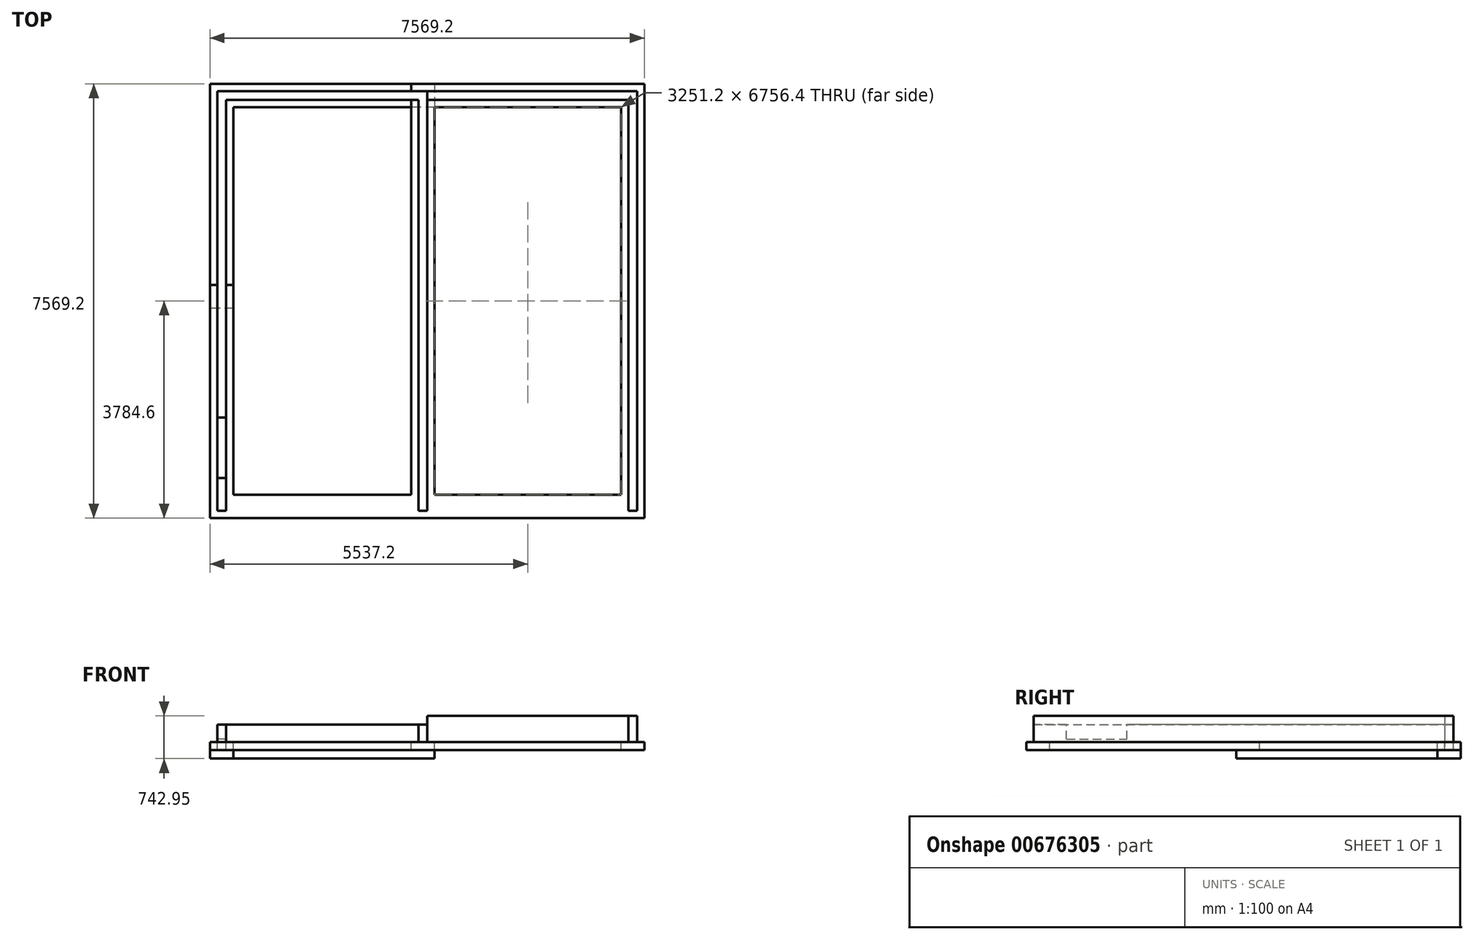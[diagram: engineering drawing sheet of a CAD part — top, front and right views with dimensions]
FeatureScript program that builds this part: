
annotation { "Feature Type Name" : "Feature", "Feature Type Description" : "" }
export const myFeature = defineFeature(function(context is Context, id is Id, definition is map)
    precondition{}
    {
        {
            var Q0;
            Q0=qCreatedBy(makeId("Top.planeOp"),FACE);
            var sketch = newSketch(context, id + "F0", { "sketchPlane" : qUnion([Q0])});
            skLineSegment(sketch, "E0.bottom", {"start": v(-3657.6, 3657.6) * mm, "end": v(3657.6, 3657.6) * mm});
            skLineSegment(sketch, "E0.top", {"start": v(-3657.6, -3657.6) * mm, "end": v(3657.6, -3657.6) * mm, "construction": true});
            skLineSegment(sketch, "E0.left", {"start": v(-3657.6, 3657.6) * mm, "end": v(-3657.6, -3657.6) * mm});
            skLineSegment(sketch, "E0.right", {"start": v(3657.6, 3657.6) * mm, "end": v(3657.6, -3657.6) * mm});
            skPoint(sketch, "E0.middle", {"position": v(0, 0) * mm});
            skLineSegment(sketch, "E1.0", {"start": v(-3505.2, 3505.2) * mm, "end": v(-3505.2, -3657.6) * mm});
            skLineSegment(sketch, "E1.1", {"start": v(-3505.2, 3505.2) * mm, "end": v(-152.4, 3505.2) * mm});
            skLineSegment(sketch, "E1.2", {"start": v(3505.2, 3505.2) * mm, "end": v(3505.2, -3657.6) * mm});
            skLineSegment(sketch, "E2", {"start": v(-3657.6, -3657.6) * mm, "end": v(-3505.2, -3657.6) * mm});
            skLineSegment(sketch, "E3", {"start": v(3657.6, -3657.6) * mm, "end": v(3505.2, -3657.6) * mm});
            skLineSegment(sketch, "E4", {"start": v(0, 3505.2) * mm, "end": v(0, -3657.6) * mm});
            skLineSegment(sketch, "E5", {"start": v(0, -3657.6) * mm, "end": v(-152.4, -3657.6) * mm});
            skLineSegment(sketch, "E6", {"start": v(-152.4, -3657.6) * mm, "end": v(-152.4, 3505.2) * mm});
            skLineSegment(sketch, "E7.trimOffspring", {"start": v(0, 3505.2) * mm, "end": v(3505.2, 3505.2) * mm});
            skSolve(sketch);
        }
        {
            var Q0;
            Q0=makeQuery(id+"F0.imprint","IMPRINT",FACE,{"disambiguationData":[TD([[makeQuery(id+"F0.imprint","IMPRINT",EDGE,{"derivedFrom":sQuery(id+"F0.wireOp",EDGE,"E0.bottom")}),-1.0]])]});
            extrude(context, id + "F1", {"entities" : qUnion([Q0]), "depth" : 152.4 * mm, "offsetDistance" : 25.4 * mm});
        }
        {
            var Q0;
            Q0=makeQuery(id+"F1.opExtrude","CAP_FACE",FACE,{"disambiguationData":[OSD([sQuery(id+"F0.wireOp",EDGE,"E0.bottom"),sQuery(id+"F0.wireOp",EDGE,"E0.left"),sQuery(id+"F0.wireOp",EDGE,"E0.right"),sQuery(id+"F0.wireOp",EDGE,"E1.0"),sQuery(id+"F0.wireOp",EDGE,"E1.1"),sQuery(id+"F0.wireOp",EDGE,"E1.2"),sQuery(id+"F0.wireOp",EDGE,"E2"),sQuery(id+"F0.wireOp",EDGE,"E3")])],"isStart":true});
            extrude(context, id + "F2", {"entities" : qUnion([Q0]), "operationType" : NewBodyOperationType.ADD, "depth" : 152.4 * mm, "offsetDistance" : 25.4 * mm});
        }
        {
            var Q0;
            Q0=makeQuery(id+"F2.opExtrude","CAP_FACE",FACE,{"disambiguationData":[OSD([sQuery(id+"F0.wireOp",EDGE,"E0.bottom"),sQuery(id+"F0.wireOp",EDGE,"E0.left"),sQuery(id+"F0.wireOp",EDGE,"E0.right"),sQuery(id+"F0.wireOp",EDGE,"E1.0"),sQuery(id+"F0.wireOp",EDGE,"E1.1"),sQuery(id+"F0.wireOp",EDGE,"E1.2"),sQuery(id+"F0.wireOp",EDGE,"E2"),sQuery(id+"F0.wireOp",EDGE,"E3")])],"isStart":false});
            var sketch = newSketch(context, id + "F3", { "sketchPlane" : qUnion([Q0])});
            skLineSegment(sketch, "E8.bottom", {"start": v(-3784.6, 3784.6) * mm, "end": v(3784.6, 3784.6) * mm});
            skLineSegment(sketch, "E8.top", {"start": v(-3784.6, -3784.6) * mm, "end": v(3784.6, -3784.6) * mm, "construction": true});
            skLineSegment(sketch, "E8.left", {"start": v(-3784.6, 3784.6) * mm, "end": v(-3784.6, -3784.6) * mm, "construction": true});
            skLineSegment(sketch, "E8.right", {"start": v(3784.6, 3784.6) * mm, "end": v(3784.6, -3784.6) * mm});
            skPoint(sketch, "E8.middle", {"position": v(0, 0) * mm});
            skLineSegment(sketch, "E9.0", {"start": v(-3378.2, 3378.2) * mm, "end": v(-279.4, 3378.2) * mm});
            skLineSegment(sketch, "E9.1", {"start": v(-3378.2, 3378.2) * mm, "end": v(-3378.2, -279.4) * mm});
            skLineSegment(sketch, "E9.3", {"start": v(3378.2, 3378.2) * mm, "end": v(3378.2, -3378.2) * mm});
            skLineSegment(sketch, "E10", {"start": v(-279.4, 3378.2) * mm, "end": v(-279.4, -3505.2) * mm});
            skLineSegment(sketch, "E11", {"start": v(127, 3378.2) * mm, "end": v(127, -3378.2) * mm});
            skLineSegment(sketch, "E12.trimOffspring", {"start": v(127, 3378.2) * mm, "end": v(3378.2, 3378.2) * mm});
            skLineSegment(sketch, "E13.trimOffspring", {"start": v(127, -3378.2) * mm, "end": v(3378.2, -3378.2) * mm});
            skLineSegment(sketch, "E14", {"start": v(-279.4, -3505.2) * mm, "end": v(-3505.2, -3505.2) * mm});
            skLineSegment(sketch, "E15", {"start": v(-3784.6, 3784.6) * mm, "end": v(-3784.6, -279.4) * mm});
            skLineSegment(sketch, "E16", {"start": v(-3784.6, -279.4) * mm, "end": v(-3657.6, -279.4) * mm});
            skLineSegment(sketch, "E17", {"start": v(-3657.6, -279.4) * mm, "end": v(-3657.6, -3657.6) * mm});
            skLineSegment(sketch, "E18", {"start": v(-3657.6, -3657.6) * mm, "end": v(-279.4, -3657.6) * mm});
            skLineSegment(sketch, "E19", {"start": v(-279.4, -3657.6) * mm, "end": v(-279.4, -3784.6) * mm});
            skLineSegment(sketch, "E20", {"start": v(-279.4, -3784.6) * mm, "end": v(3784.6, -3784.6) * mm});
            skLineSegment(sketch, "E21", {"start": v(-3505.2, -279.4) * mm, "end": v(-3378.2, -279.4) * mm});
            skLineSegment(sketch, "E22", {"start": v(-3505.2, -279.4) * mm, "end": v(-3505.2, -3505.2) * mm});
            skSolve(sketch);
        }
        {
            var Q0;
            Q0 = qSketchRegion(id + "F3", true);
            extrude(context, id + "F4", {"entities" : qUnion([Q0]), "operationType" : NewBodyOperationType.ADD, "depth" : 139.7 * mm, "offsetDistance" : 25.4 * mm});
        }
        {
            var Q0;
            Q0=makeQuery(id+"F1.opExtrude","CAP_FACE",FACE,{"disambiguationData":[OSD([sQuery(id+"F0.wireOp",EDGE,"E0.bottom"),sQuery(id+"F0.wireOp",EDGE,"E0.left"),sQuery(id+"F0.wireOp",EDGE,"E0.right"),sQuery(id+"F0.wireOp",EDGE,"E1.0"),sQuery(id+"F0.wireOp",EDGE,"E1.1"),sQuery(id+"F0.wireOp",EDGE,"E1.2"),sQuery(id+"F0.wireOp",EDGE,"E2"),sQuery(id+"F0.wireOp",EDGE,"E3"),sQuery(id+"F0.wireOp",EDGE,"E4"),sQuery(id+"F0.wireOp",EDGE,"E5"),sQuery(id+"F0.wireOp",EDGE,"E6"),sQuery(id+"F0.wireOp",EDGE,"E7.trimOffspring")])],"isStart":false});
            var sketch = newSketch(context, id + "F5", { "sketchPlane" : qUnion([Q0])});
            skLineSegment(sketch, "E23", {"start": v(0, 3657.6) * mm, "end": v(3657.6, 3657.6) * mm});
            skLineSegment(sketch, "E24", {"start": v(3657.6, 3657.6) * mm, "end": v(3657.6, -3657.6) * mm});
            skLineSegment(sketch, "E25", {"start": v(3657.6, -3657.6) * mm, "end": v(3505.2, -3657.6) * mm});
            skLineSegment(sketch, "E26", {"start": v(3505.2, -3657.6) * mm, "end": v(3505.2, 3505.2) * mm});
            skLineSegment(sketch, "E27", {"start": v(3505.2, 3505.2) * mm, "end": v(0, 3505.2) * mm});
            skLineSegment(sketch, "E28", {"start": v(0, 3505.2) * mm, "end": v(0, 3657.6) * mm});
            skSolve(sketch);
        }
        {
            var Q0;
            Q0=makeQuery(id+"F4.opExtrude","CAP_FACE",FACE,{"disambiguationData":[OSD([sQuery(id+"F3.wireOp",EDGE,"E8.bottom"),sQuery(id+"F3.wireOp",EDGE,"E8.right"),sQuery(id+"F3.wireOp",EDGE,"E9.0"),sQuery(id+"F3.wireOp",EDGE,"E9.1"),sQuery(id+"F3.wireOp",EDGE,"E9.3"),sQuery(id+"F3.wireOp",EDGE,"E10"),sQuery(id+"F3.wireOp",EDGE,"E11"),sQuery(id+"F3.wireOp",EDGE,"E12.trimOffspring"),sQuery(id+"F3.wireOp",EDGE,"E13.trimOffspring"),sQuery(id+"F3.wireOp",EDGE,"E14"),sQuery(id+"F3.wireOp",EDGE,"E15"),sQuery(id+"F3.wireOp",EDGE,"E16"),sQuery(id+"F3.wireOp",EDGE,"E17"),sQuery(id+"F3.wireOp",EDGE,"E18"),sQuery(id+"F3.wireOp",EDGE,"E19"),sQuery(id+"F3.wireOp",EDGE,"E20"),sQuery(id+"F3.wireOp",EDGE,"E21"),sQuery(id+"F3.wireOp",EDGE,"E22")])],"isStart":false});
            var sketch = newSketch(context, id + "F6", { "sketchPlane" : qUnion([Q0])});
            skLineSegment(sketch, "E29", {"start": v(-3784.6, 127) * mm, "end": v(-3784.6, -3784.6) * mm});
            skLineSegment(sketch, "E30", {"start": v(-3784.6, -3784.6) * mm, "end": v(127, -3784.6) * mm});
            skLineSegment(sketch, "E31", {"start": v(127, -3784.6) * mm, "end": v(127, -3378.2) * mm});
            skLineSegment(sketch, "E32", {"start": v(127, -3378.2) * mm, "end": v(-3378.2, -3378.2) * mm});
            skLineSegment(sketch, "E33", {"start": v(-3378.2, -3378.2) * mm, "end": v(-3378.2, 127) * mm});
            skLineSegment(sketch, "E34", {"start": v(-3378.2, 127) * mm, "end": v(-3784.6, 127) * mm});
            skSolve(sketch);
        }
        {
            var Q0;
            Q0 = qSketchRegion(id + "F6", true);
            extrude(context, id + "F7", {"entities" : qUnion([Q0]), "operationType" : NewBodyOperationType.ADD, "depth" : 146.05 * mm, "offsetDistance" : 25.4 * mm});
        }
        {
            var Q0;
            Q0 = qSketchRegion(id + "F5", true);
            extrude(context, id + "F8", {"entities" : qUnion([Q0]), "operationType" : NewBodyOperationType.ADD, "depth" : 152.4 * mm, "offsetDistance" : 25.4 * mm});
        }
        {
            var Q0;
            {var subQ0=sQuery(id+"F0.wireOp",EDGE,"E5");Q0=makeQuery(id+"F2.boolean.opBoolean","MERGE",FACE,{"derivedFrom":[makeQuery(id+"F1.opExtrude","SWEPT_FACE",FACE,{"disambiguationData":[OSD([subQ0])]}),makeQuery(id+"F2.opExtrude","SWEPT_FACE",FACE,{"disambiguationData":[OSD([subQ0])]})]});}
            var sketch = newSketch(context, id + "F9", { "sketchPlane" : qUnion([Q0])});
            skLineSegment(sketch, "E35", {"start": v(0, 107.95) * mm, "end": v(-3657.6, -25.4) * mm});
            skLineSegment(sketch, "E36", {"start": v(-3657.6, -25.4) * mm, "end": v(3657.6, -25.4) * mm});
            skLineSegment(sketch, "E37", {"start": v(3657.6, -25.4) * mm, "end": v(3657.6, 273.05) * mm});
            skLineSegment(sketch, "E38", {"start": v(3657.6, 273.05) * mm, "end": v(0, 107.95) * mm});
            skSolve(sketch);
        }
        {
            var Q0;
            {var subQ0=sQuery(id+"F0.wireOp",EDGE,"E0.right");Q0=makeQuery(id+"F8.boolean.opBoolean","MERGE",FACE,{"derivedFrom":[makeQuery(id+"F2.boolean.opBoolean","MERGE",FACE,{"derivedFrom":[makeQuery(id+"F1.opExtrude","SWEPT_FACE",FACE,{"disambiguationData":[OSD([subQ0])]}),makeQuery(id+"F2.opExtrude","SWEPT_FACE",FACE,{"disambiguationData":[OSD([subQ0])]})]}),makeQuery(id+"F8.opExtrude","SWEPT_FACE",FACE,{"disambiguationData":[OSD([sQuery(id+"F5.wireOp",EDGE,"E24")])]})]});}
            var sketch = newSketch(context, id + "F10", { "sketchPlane" : qUnion([Q0])});
            skLineSegment(sketch, "E39", {"start": v(-3657.6, -25.4) * mm, "end": v(3657.6, -25.4) * mm});
            skLineSegment(sketch, "E40", {"start": v(3657.6, -25.4) * mm, "end": v(3657.6, 158.75) * mm});
            skLineSegment(sketch, "E41", {"start": v(3657.6, 158.75) * mm, "end": v(0, 196.85) * mm});
            skLineSegment(sketch, "E42", {"start": v(0, 196.85) * mm, "end": v(-3657.6, 273.05) * mm});
            skLineSegment(sketch, "E43", {"start": v(-3657.6, 273.05) * mm, "end": v(-3657.6, -25.4) * mm});
            skLineSegment(sketch, "E44", {"start": v(0, 196.85) * mm, "end": v(0, -25.4) * mm});
            skSolve(sketch);
        }
        {
            var Q0;
            {var subQ0=sQuery(id+"F0.wireOp",EDGE,"E0.left");Q0=makeQuery(id+"F4.boolean.opBoolean","MERGE",FACE,{"derivedFrom":[makeQuery(id+"F2.boolean.opBoolean","MERGE",FACE,{"derivedFrom":[makeQuery(id+"F1.opExtrude","SWEPT_FACE",FACE,{"disambiguationData":[OSD([subQ0])]}),makeQuery(id+"F2.opExtrude","SWEPT_FACE",FACE,{"disambiguationData":[OSD([subQ0])]})]}),makeQuery(id+"F4.opExtrude","SWEPT_FACE",FACE,{"disambiguationData":[OSD([sQuery(id+"F3.wireOp",EDGE,"E17")])]})]});}
            var sketch = newSketch(context, id + "F11", { "sketchPlane" : qUnion([Q0])});
            skLineSegment(sketch, "E45", {"start": v(3657.6, -25.4) * mm, "end": v(0, -88.9) * mm});
            skLineSegment(sketch, "E46", {"start": v(0, -88.9) * mm, "end": v(-3657.6, -139.7) * mm});
            skLineSegment(sketch, "E47", {"start": v(-3657.6, -139.7) * mm, "end": v(-3657.6, -25.4) * mm});
            skLineSegment(sketch, "E48", {"start": v(-3657.6, -25.4) * mm, "end": v(3657.6, -25.4) * mm});
            skLineSegment(sketch, "E49", {"start": v(0, -88.9) * mm, "end": v(0, -25.4) * mm});
            skSolve(sketch);
        }
        {
            var Q0;
            {var subQ1=sQuery(id+"F0.wireOp",EDGE,"E0.left");var subQ3=makeQuery(id+"F1.opExtrude","CAP_EDGE",EDGE,{"disambiguationData":[OSD([subQ1])],"isStart":false});Q0=makeQuery(id+"F11.imprint","IMPRINT",FACE,{"disambiguationData":[TD([[makeQuery(id+"F11.imprint","IMPRINT",EDGE,{"derivedFrom":subQ3}),-1.0]])]});}
            var sketch = newSketch(context, id + "F12", { "sketchPlane" : qUnion([Q0])});
            skLineSegment(sketch, "E50.bottom", {"start": v(2032, 152.4) * mm, "end": v(3086.1, 152.4) * mm});
            skLineSegment(sketch, "E50.top", {"start": v(2032, -101.6) * mm, "end": v(3086.1, -101.6) * mm});
            skLineSegment(sketch, "E50.left", {"start": v(2032, 152.4) * mm, "end": v(2032, -101.6) * mm});
            skLineSegment(sketch, "E50.right", {"start": v(3086.1, 152.4) * mm, "end": v(3086.1, -101.6) * mm});
            skSolve(sketch);
        }
        {
            var Q0;
            Q0 = qSketchRegion(id + "F12", true);
            extrude(context, id + "F13", {"entities" : qUnion([Q0]), "operationType" : NewBodyOperationType.REMOVE, "oppositeDirection" : true, "depth" : 284.48 * mm, "offsetDistance" : 25.4 * mm});
        }
    });
